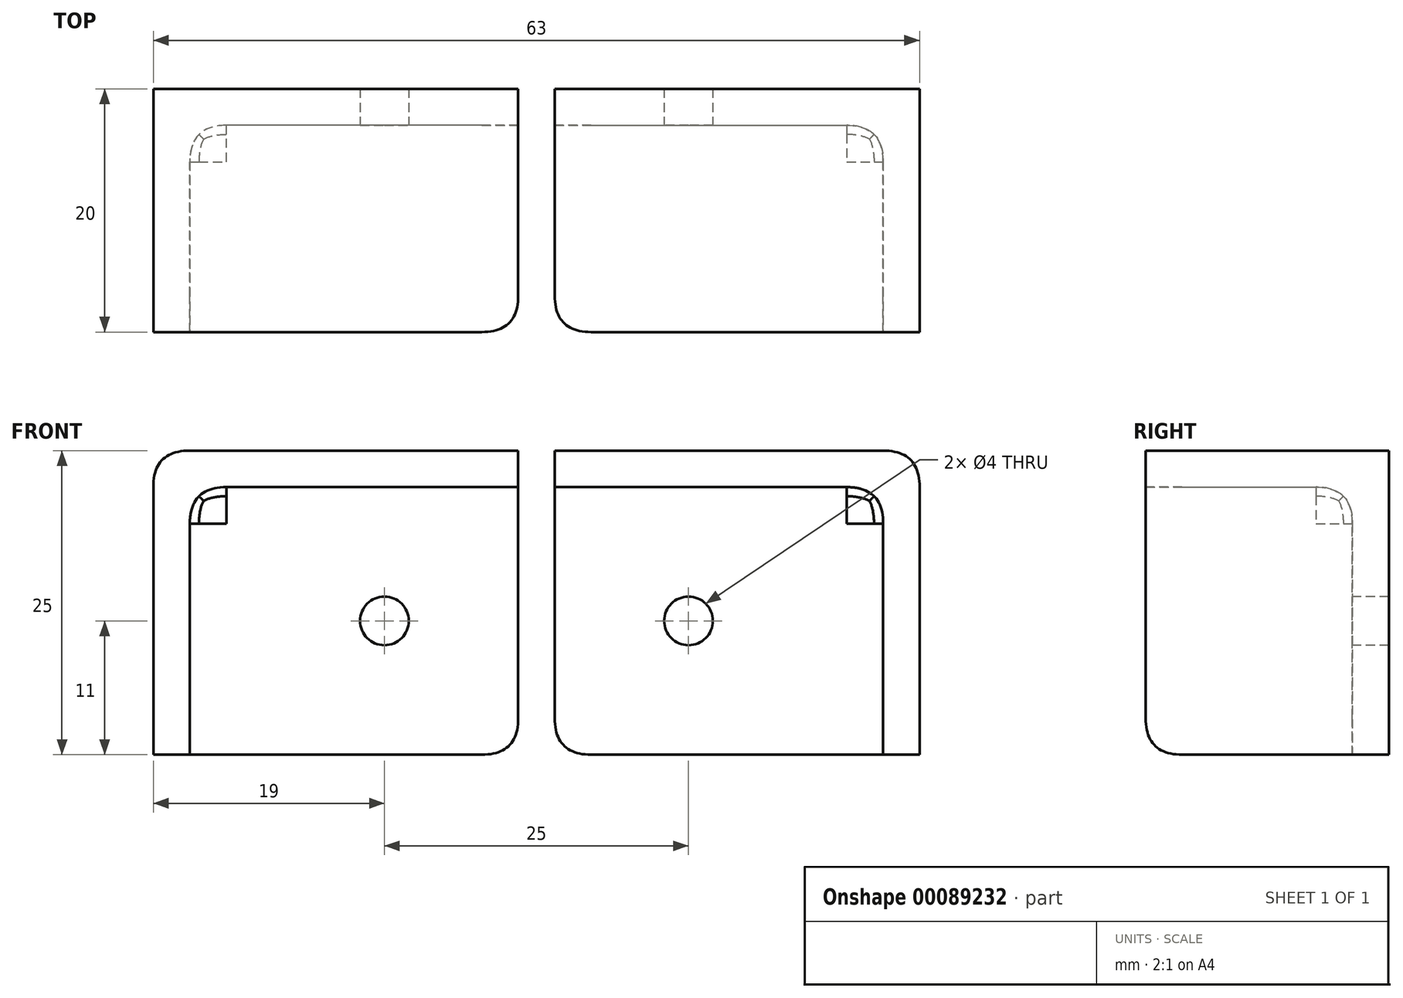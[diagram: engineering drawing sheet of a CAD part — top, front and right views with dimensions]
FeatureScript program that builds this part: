
annotation { "Feature Type Name" : "Feature", "Feature Type Description" : "" }
export const myFeature = defineFeature(function(context is Context, id is Id, definition is map)
    precondition{}
    {
        {
            var Q0;
            Q0=qCreatedBy(makeId("Front.planeOp"),FACE);
            var sketch = newSketch(context, id + "F0", { "sketchPlane" : qUnion([Q0])});
            skLineSegment(sketch, "E0.bottom", {"start": v(15, -12.5) * mm, "end": v(-15, -12.5) * mm});
            skLineSegment(sketch, "E0.top", {"start": v(15, 12.5) * mm, "end": v(-15, 12.5) * mm});
            skLineSegment(sketch, "E0.left", {"start": v(15, -12.5) * mm, "end": v(15, 12.5) * mm});
            skLineSegment(sketch, "E0.right", {"start": v(-15, -12.5) * mm, "end": v(-15, 12.5) * mm});
            skLineSegment(sketch, "E1", {"start": v(-15, 12.5) * mm, "end": v(15, -12.5) * mm, "construction": true});
            skSolve(sketch);
        }
        {
            assignVariable(context, id + "F1", {"name" : "t", "anyValue" : 3});
        }
        {
            var Q0;
            Q0 = qSketchRegion(id + "F0", true);
            extrude(context, id + "F2", {"entities" : qUnion([Q0]), "depth" : 20 * mm});
        }
        {
            var Q0;
            Q0=makeQuery(id+"F2.opExtrude","CAP_FACE",FACE,{"disambiguationData":[OSD([sQuery(id+"F0.wireOp",EDGE,"E0.bottom"),sQuery(id+"F0.wireOp",EDGE,"E0.top"),sQuery(id+"F0.wireOp",EDGE,"E0.left"),sQuery(id+"F0.wireOp",EDGE,"E0.right")])],"isStart":true});
            cPlane(context, id + "F3", {"entities" : qUnion([Q0]), "cplaneType" : CPlaneType.OFFSET, "offset" : (getVariable(context, 't')) * mm, "oppositeDirection" : true, "width" : 150 * mm, "height" : 150 * mm});
        }
        {
            var Q0;
            Q0=qCreatedBy(id+"F3.planeOp",FACE);
            var sketch = newSketch(context, id + "F4", { "sketchPlane" : qUnion([Q0])});
            skLineSegment(sketch, "E2.bottom", {"start": v(-15, -12.5) * mm, "end": v(12, -12.5) * mm});
            skLineSegment(sketch, "E2.top", {"start": v(-15, 9.5) * mm, "end": v(12, 9.5) * mm});
            skLineSegment(sketch, "E2.left", {"start": v(-15, -12.5) * mm, "end": v(-15, 9.5) * mm});
            skLineSegment(sketch, "E2.right", {"start": v(12, -12.5) * mm, "end": v(12, 9.5) * mm});
            skSolve(sketch);
        }
        {
            var Q0;
            Q0 = qSketchRegion(id + "F4", true);
            var Q1;
            Q1=makeQuery(id+"F2.opExtrude","CAP_FACE",FACE,{"disambiguationData":[OSD([sQuery(id+"F0.wireOp",EDGE,"E0.bottom"),sQuery(id+"F0.wireOp",EDGE,"E0.top"),sQuery(id+"F0.wireOp",EDGE,"E0.left"),sQuery(id+"F0.wireOp",EDGE,"E0.right")])],"isStart":true});
            extrude(context, id + "F5", {"entities" : qUnion([Q0]), "operationType" : NewBodyOperationType.REMOVE, "oppositeDirection" : true, "endBoundEntityFace" : qUnion([Q1]), "depth" : 18 * mm});
        }
        {
            var Q0;
            Q0=makeQuery(id+"F5.boolean.opBoolean","COPY",FACE,{"derivedFrom":makeQuery(id+"F5.opExtrude","CAP_FACE",FACE,{"disambiguationData":[OSD([sQuery(id+"F4.wireOp",EDGE,"E2.bottom"),sQuery(id+"F4.wireOp",EDGE,"E2.top"),sQuery(id+"F4.wireOp",EDGE,"E2.left"),sQuery(id+"F4.wireOp",EDGE,"E2.right")])],"isStart":true})});
            var sketch = newSketch(context, id + "F6", { "sketchPlane" : qUnion([Q0])});
            skLineSegment(sketch, "E3", {"start": v(15, -1.5) * mm, "end": v(4, -1.5) * mm, "construction": true});
            skLineSegment(sketch, "E4", {"start": v(4, -1.5) * mm, "end": v(4, -12.5) * mm, "construction": true});
            skCircle(sketch, "E5", {"center": v(4, -1.5) * mm, "radius": 2 * mm});
            skSolve(sketch);
        }
        {
            var Q0;
            Q0 = qSketchRegion(id + "F6", true);
            extrude(context, id + "F7", {"entities" : qUnion([Q0]), "operationType" : NewBodyOperationType.REMOVE, "endBound" : BoundingType.THROUGH_ALL, "oppositeDirection" : true, "depth" : 25 * mm});
        }
        {
            var Q0;
            Q0=makeQuery(id+"F5.boolean.opBoolean","COPY",EDGE,{"derivedFrom":makeQuery(id+"F5.opExtrude","CAP_EDGE",EDGE,{"disambiguationData":[OSD([sQuery(id+"F4.wireOp",EDGE,"E2.right")])],"isStart":true})});
            var Q1;
            Q1=makeQuery(id+"F5.boolean.opBoolean","COPY",EDGE,{"derivedFrom":makeQuery(id+"F5.opExtrude","CAP_EDGE",EDGE,{"disambiguationData":[OSD([sQuery(id+"F4.wireOp",EDGE,"E2.top")])],"isStart":true})});
            var Q2;
            Q2=makeQuery(id+"F2.opExtrude","CAP_EDGE",EDGE,{"disambiguationData":[OSD([sQuery(id+"F0.wireOp",EDGE,"E0.bottom")])],"isStart":false});
            var Q3;
            Q3=makeQuery(id+"F2.opExtrude","CAP_EDGE",EDGE,{"disambiguationData":[OSD([sQuery(id+"F0.wireOp",EDGE,"E0.left")])],"isStart":false});
            var Q4;
            Q4=makeQuery(id+"F2.opExtrude","SWEPT_EDGE",EDGE,{"disambiguationData":[OSD([sQuery(id+"F0.wireOp",EDGE,"E0.bottom"),sQuery(id+"F0.wireOp",EDGE,"E0.left")])]});
            var Q5;
            Q5=makeQuery(id+"F5.boolean.opBoolean","COPY",EDGE,{"derivedFrom":makeQuery(id+"F5.opExtrude","SWEPT_EDGE",EDGE,{"disambiguationData":[OSD([sQuery(id+"F4.wireOp",EDGE,"E2.top"),sQuery(id+"F4.wireOp",EDGE,"E2.right")])]})});
            var Q6;
            Q6=makeQuery(id+"F2.opExtrude","SWEPT_EDGE",EDGE,{"disambiguationData":[OSD([sQuery(id+"F0.wireOp",EDGE,"E0.top"),sQuery(id+"F0.wireOp",EDGE,"E0.right")])]});
            fillet(context, id + "F8", {"entities" : qUnion([Q0, Q1, Q2, Q3, Q4, Q5, Q6]), "radius" : (getVariable(context, 't')) * mm, "tangentPropagation" : true, "rho" : 0.5, "crossSection" : FilletCrossSection.CONIC, "allowEdgeOverflow" : false});
        }
        {
            var Q0;
            Q0=makeQuery(id+"F2.opExtrude","SWEPT_BODY",BODY,{"disambiguationData":[OSD([sQuery(id+"F0.wireOp",EDGE,"E0.bottom"),sQuery(id+"F0.wireOp",EDGE,"E0.top"),sQuery(id+"F0.wireOp",EDGE,"E0.left"),sQuery(id+"F0.wireOp",EDGE,"E0.right")])]});
            var Q1;
            Q1=makeQuery(id+"F2.opExtrude","SWEPT_FACE",FACE,{"disambiguationData":[OSD([sQuery(id+"F0.wireOp",EDGE,"E0.left")])]});
            mirror(context, id + "F9", {"entities" : qUnion([Q0]), "mirrorPlane" : qUnion([Q1])});
        }
        {
            var Q0;
            Q0=makeQuery(id+"F9.opPattern","COPY",BODY,{"derivedFrom":makeQuery(id+"F2.opExtrude","SWEPT_BODY",BODY,{"disambiguationData":[OSD([sQuery(id+"F0.wireOp",EDGE,"E0.bottom"),sQuery(id+"F0.wireOp",EDGE,"E0.top"),sQuery(id+"F0.wireOp",EDGE,"E0.left"),sQuery(id+"F0.wireOp",EDGE,"E0.right")])]}),"instanceName":"1"});
            var Q1;
            Q1=makeQuery(id+"F9.opPattern","COPY",EDGE,{"derivedFrom":makeQuery(id+"F5.boolean.opBoolean","INTERSECT",EDGE,{"derivedFrom":[makeQuery(id+"F2.opExtrude","CAP_FACE",FACE,{"disambiguationData":[OSD([sQuery(id+"F0.wireOp",EDGE,"E0.bottom"),sQuery(id+"F0.wireOp",EDGE,"E0.top"),sQuery(id+"F0.wireOp",EDGE,"E0.left"),sQuery(id+"F0.wireOp",EDGE,"E0.right")])],"isStart":false}),makeQuery(id+"F5.opExtrude","SWEPT_FACE",FACE,{"disambiguationData":[OSD([sQuery(id+"F4.wireOp",EDGE,"E2.top")])]})]}),"instanceName":"1"});
            var Q2;
            Q2=makeQuery(id+"F9.opPattern","COPY",EDGE,{"derivedFrom":makeQuery(id+"F5.boolean.opBoolean","INTERSECT",EDGE,{"derivedFrom":[makeQuery(id+"F2.opExtrude","CAP_FACE",FACE,{"disambiguationData":[OSD([sQuery(id+"F0.wireOp",EDGE,"E0.bottom"),sQuery(id+"F0.wireOp",EDGE,"E0.top"),sQuery(id+"F0.wireOp",EDGE,"E0.left"),sQuery(id+"F0.wireOp",EDGE,"E0.right")])],"isStart":false}),makeQuery(id+"F5.opExtrude","SWEPT_FACE",FACE,{"disambiguationData":[OSD([sQuery(id+"F4.wireOp",EDGE,"E2.top")])]})]}),"instanceName":"1"});
            transform(context, id + "F10", {"entities" : qUnion([Q0]), "transformType" : TransformType.TRANSLATION_DISTANCE, "transformDirection" : qUnion([Q2]), "distance" : (getVariable(context, 't')) * mm, "oppositeDirection" : true, "makeCopy" : false});
        }
    });
